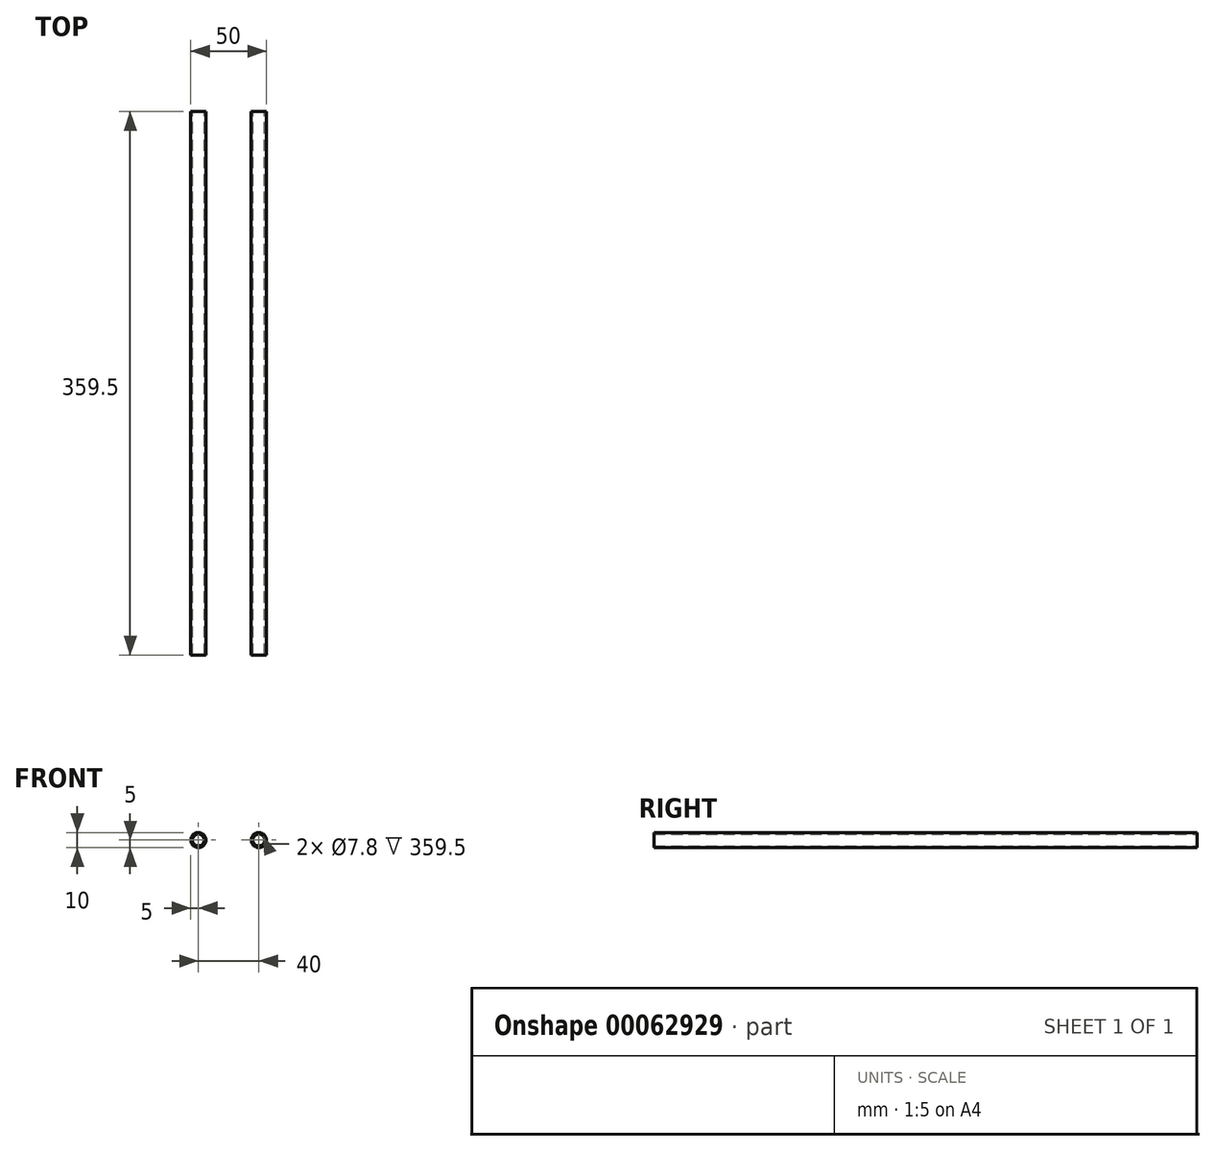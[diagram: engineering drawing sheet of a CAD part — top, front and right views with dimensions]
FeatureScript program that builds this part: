
annotation { "Feature Type Name" : "Feature", "Feature Type Description" : "" }
export const myFeature = defineFeature(function(context is Context, id is Id, definition is map)
    precondition{}
    {
        {
            var Q0;
            Q0=qCreatedBy(makeId("Front.planeOp"),FACE);
            var sketch = newSketch(context, id + "F0", { "sketchPlane" : qUnion([Q0])});
            skCircle(sketch, "E0", {"center": v(-20, 0) * mm, "radius": 5 * mm});
            skCircle(sketch, "E1", {"center": v(20, 0) * mm, "radius": 5 * mm});
            skCircle(sketch, "E2", {"center": v(-20, 0) * mm, "radius": 3.9 * mm});
            skCircle(sketch, "E3", {"center": v(20, 0) * mm, "radius": 3.9 * mm});
            skSolve(sketch);
        }
        {
            var Q0;
            Q0=makeQuery(id+"F0.imprint","IMPRINT",FACE,{"disambiguationData":[TD([[makeQuery(id+"F0.imprint","IMPRINT",EDGE,{"derivedFrom":sQuery(id+"F0.wireOp",EDGE,"E0")}),1.0]])]});
            var Q1;
            Q1=makeQuery(id+"F0.imprint","IMPRINT",FACE,{"disambiguationData":[TD([[makeQuery(id+"F0.imprint","IMPRINT",EDGE,{"derivedFrom":sQuery(id+"F0.wireOp",EDGE,"E1")}),1.0]])]});
            extrude(context, id + "F1", {"entities" : qUnion([Q0, Q1]), "depth" : 359.5 * mm});
        }
    });
